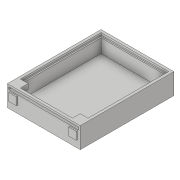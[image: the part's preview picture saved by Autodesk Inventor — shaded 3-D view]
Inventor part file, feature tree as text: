
AUTODESK INVENTOR PART (.ipt)
format: ipt  version: 2018.3 (Build 223284000, 284)  size: 151,552 bytes
history: native  units: in
note: dims shown in document units (in); Inventor stores cm internally (conversion verified against a paired STEP export)
features: extrude x5, sketch x5
ambient origin geometry x8: Origin, YZ Plane, XZ Plane, XY Plane, X Axis, Y Axis, Z Axis, Center Point
bodies: Solid1 (feature_tree)
feature tree (10):
  extrude  "Extrusion1"  Depth=1.0in
  extrude  "Extrusion2"  Depth=0.125in
  extrude  "Extrusion3"  Depth=0.125in
  extrude  "Extrusion4"  Depth=0.875in TaperAngle=0.0deg
  extrude  "Extrusion5"  Depth=0.0625in
  sketch  "Sketch1"  dims[d0=3.5in d1=1.0in]
  sketch  "Sketch2"  dims[d2=4.5in d3=0.0in d4=0.125in]
  sketch  "Sketch3"  dims[d5=0.125in d6=0.125in]
  sketch  "Sketch5"  dims[d7=0.125in d8=0.875in d9=0.0in]
  sketch  "Sketch6"  dims[d46=0.125in d47=0.0625in d49=0.0625in d50=4.4375in d51=0.0in d62=0.25in d64=0.375in d65=0.25in d66=0.0in d67=0.375in d68=0.375in d69=0.375in d70=0.375in d71=0.375in d72=0.375in d73=0.375in d74=0.0625in d75=0.0in d76=0.052in d77=0.052in d78=0.125in d79=0.125in]
